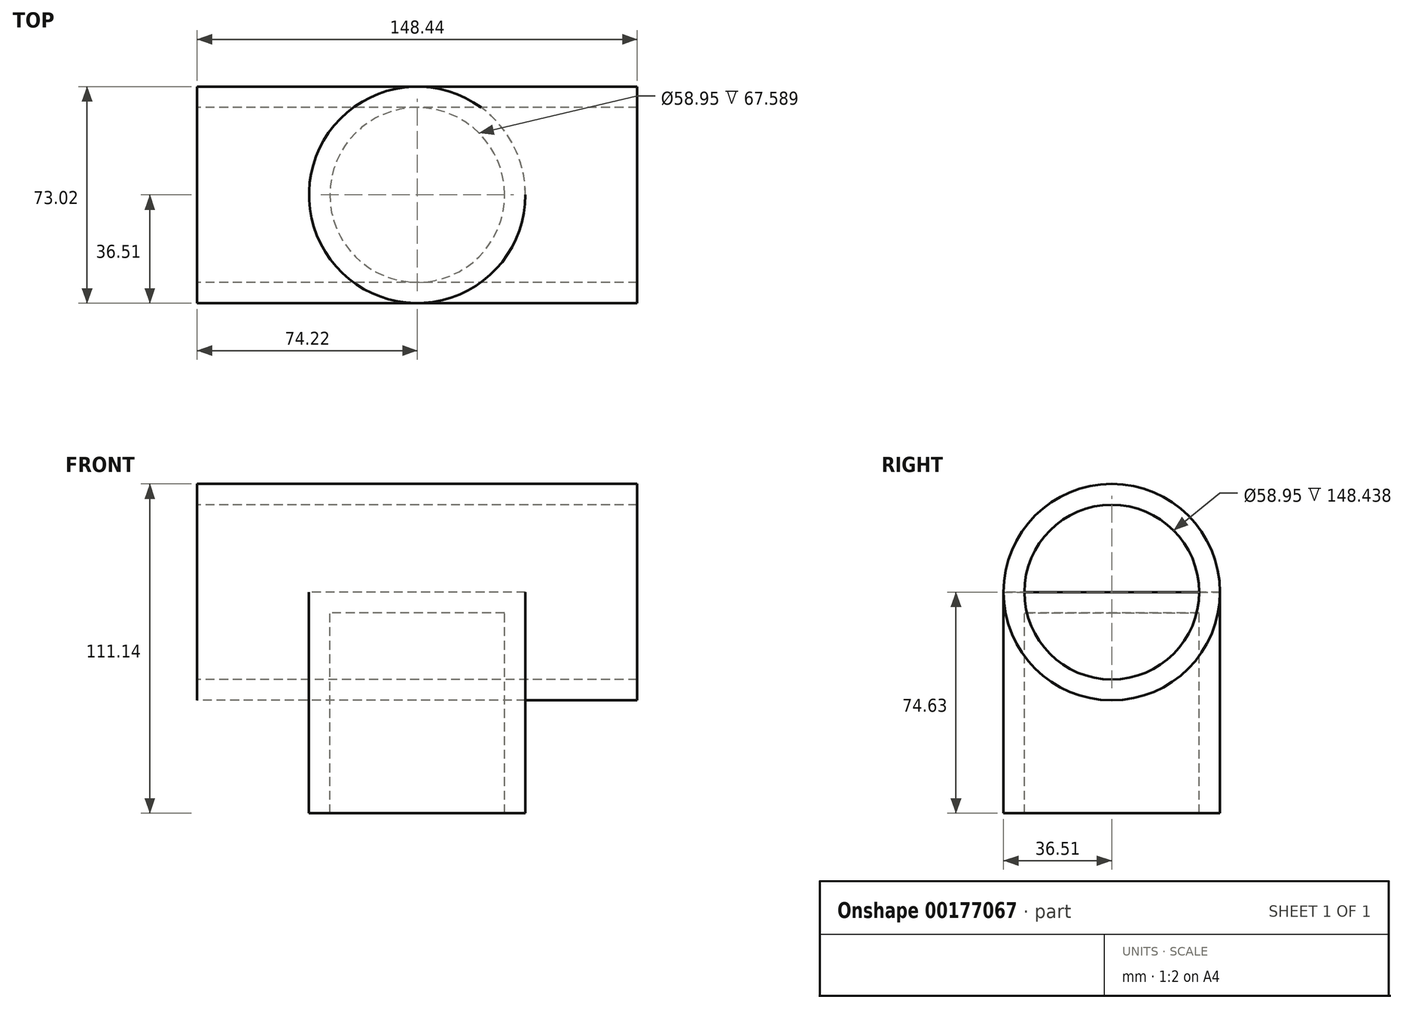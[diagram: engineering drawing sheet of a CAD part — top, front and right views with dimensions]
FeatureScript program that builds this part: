
annotation { "Feature Type Name" : "Feature", "Feature Type Description" : "" }
export const myFeature = defineFeature(function(context is Context, id is Id, definition is map)
    precondition{}
    {
        {
            var Q0;
            Q0=qCreatedBy(makeId("Right.planeOp"),FACE);
            var sketch = newSketch(context, id + "F0", { "sketchPlane" : qUnion([Q0])});
            skCircle(sketch, "E0", {"center": v(0, 0) * mm, "radius": 36.51 * mm});
            skSolve(sketch);
        }
        {
            var Q0;
            Q0=makeQuery(id+"F0.imprint","IMPRINT",FACE,{"disambiguationData":[TD([[makeQuery(id+"F0.imprint","IMPRINT",EDGE,{"derivedFrom":sQuery(id+"F0.wireOp",EDGE,"E0")}),1.0]])]});
            extrude(context, id + "F1", {"entities" : qUnion([Q0]), "depth" : 148.44 * mm, "symmetric" : true});
        }
        {
            var Q0;
            Q0=qCreatedBy(makeId("Top.planeOp"),FACE);
            var sketch = newSketch(context, id + "F2", { "sketchPlane" : qUnion([Q0])});
            skCircle(sketch, "E1", {"center": v(0, 0) * mm, "radius": 36.51 * mm});
            skSolve(sketch);
        }
        {
            var Q0;
            Q0=makeQuery(id+"F2.imprint","IMPRINT",FACE,{"disambiguationData":[TD([[makeQuery(id+"F2.imprint","IMPRINT",EDGE,{"derivedFrom":sQuery(id+"F2.wireOp",EDGE,"E1")}),1.0]])]});
            extrude(context, id + "F3", {"entities" : qUnion([Q0]), "oppositeDirection" : true, "depth" : 74.63 * mm});
        }
        {
            var Q0;
            Q0=makeQuery(id+"F1.opExtrude","CAP_FACE",FACE,{"disambiguationData":[OSD([sQuery(id+"F0.wireOp",EDGE,"E0")])],"isStart":false});
            var Q1;
            Q1=makeQuery(id+"F1.opExtrude","CAP_FACE",FACE,{"disambiguationData":[OSD([sQuery(id+"F0.wireOp",EDGE,"E0")])],"isStart":true});
            var Q2;
            Q2=makeQuery(id+"F3.opExtrude","CAP_FACE",FACE,{"disambiguationData":[OSD([sQuery(id+"F2.wireOp",EDGE,"E1")])],"isStart":false});
            shell(context, id + "F4", {"entities" : qUnion([Q0, Q1, Q2]), "thickness" : 7.04 * mm});
        }
    });
